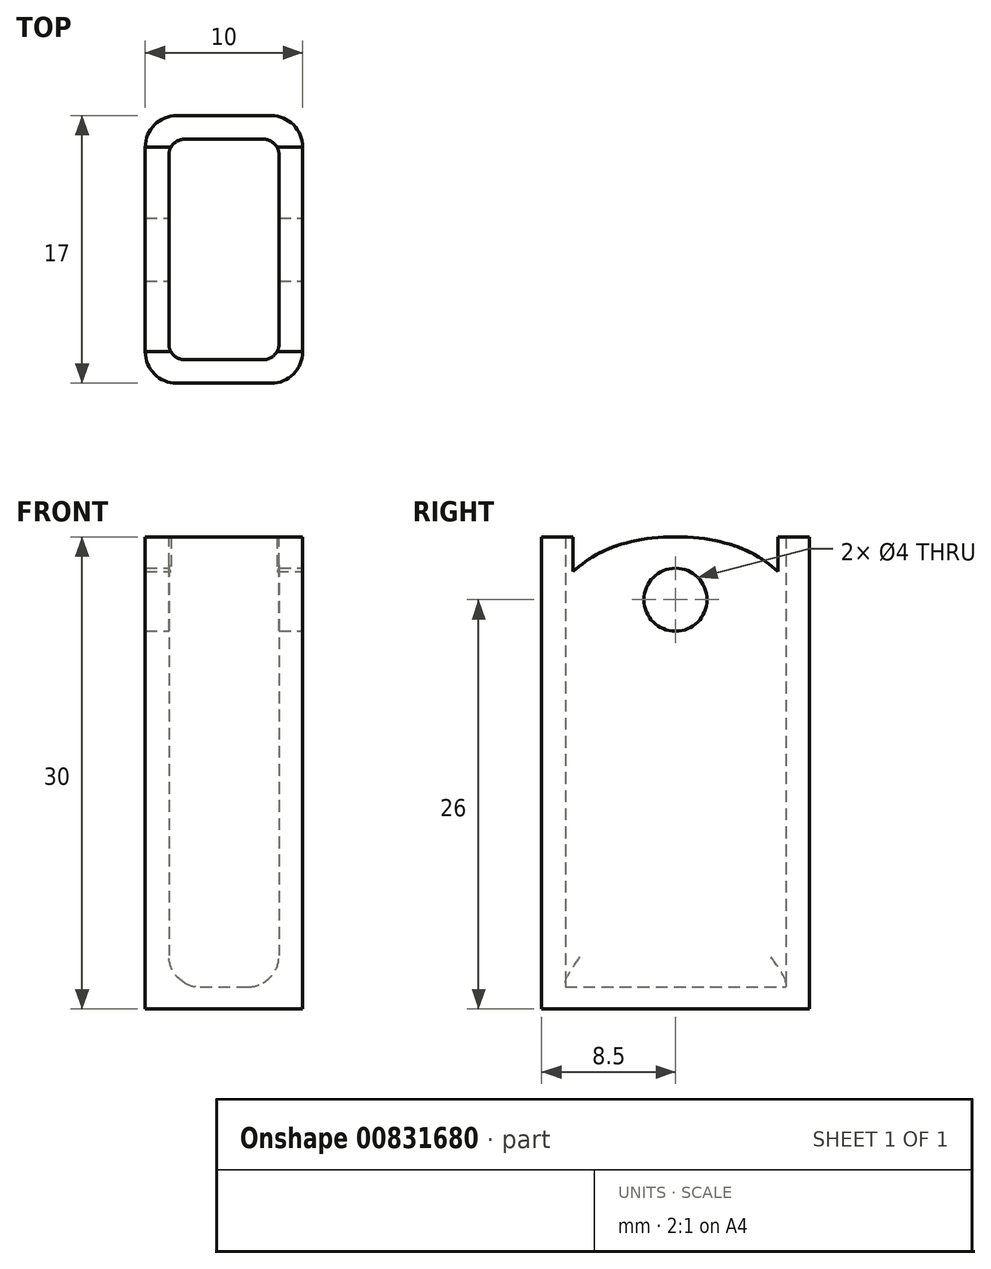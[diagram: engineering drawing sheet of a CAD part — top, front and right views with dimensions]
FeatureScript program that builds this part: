
annotation { "Feature Type Name" : "Feature", "Feature Type Description" : "" }
export const myFeature = defineFeature(function(context is Context, id is Id, definition is map)
    precondition{}
    {
        {
            var Q0;
            Q0=qCreatedBy(makeId("Top.planeOp"),FACE);
            var sketch = newSketch(context, id + "F0", { "sketchPlane" : qUnion([Q0])});
            skLineSegment(sketch, "E0.bottom", {"start": v(2.5, 7) * mm, "end": v(-2.5, 7) * mm});
            skLineSegment(sketch, "E0.top", {"start": v(2.5, -7) * mm, "end": v(-2.5, -7) * mm});
            skLineSegment(sketch, "E0.left", {"start": v(3.5, 6) * mm, "end": v(3.5, -6) * mm});
            skLineSegment(sketch, "E0.right", {"start": v(-3.5, 6) * mm, "end": v(-3.5, -6) * mm});
            skPoint(sketch, "E0.middle", {"position": v(0, 0) * mm});
            skLineSegment(sketch, "E1.0", {"start": v(3, 8.5) * mm, "end": v(-3, 8.5) * mm});
            skLineSegment(sketch, "E1.1", {"start": v(5, 6.5) * mm, "end": v(5, -6.5) * mm});
            skLineSegment(sketch, "E1.2", {"start": v(3, -8.5) * mm, "end": v(-3, -8.5) * mm});
            skLineSegment(sketch, "E1.3", {"start": v(-5, 6.5) * mm, "end": v(-5, -6.5) * mm});
            skPoint(sketch, "E2.visualSharp", {"position": v(-5, 8.5) * mm});
            skArc(sketch, "E2.filletArc", {"start": v(-3, 8.5) * mm, "mid": v(-4.41, 7.91) * mm, "end": v(-5, 6.5) * mm});
            skPoint(sketch, "E3.visualSharp", {"position": v(5, 8.5) * mm});
            skArc(sketch, "E3.filletArc", {"start": v(5, 6.5) * mm, "mid": v(4.41, 7.91) * mm, "end": v(3, 8.5) * mm});
            skPoint(sketch, "E4.visualSharp", {"position": v(5, -8.5) * mm});
            skArc(sketch, "E4.filletArc", {"start": v(3, -8.5) * mm, "mid": v(4.41, -7.91) * mm, "end": v(5, -6.5) * mm});
            skPoint(sketch, "E5.visualSharp", {"position": v(-5, -8.5) * mm});
            skArc(sketch, "E5.filletArc", {"start": v(-5, -6.5) * mm, "mid": v(-4.41, -7.91) * mm, "end": v(-3, -8.5) * mm});
            skPoint(sketch, "E6.visualSharp", {"position": v(3.5, -7) * mm});
            skArc(sketch, "E6.filletArc", {"start": v(2.5, -7) * mm, "mid": v(3.2, -6.7) * mm, "end": v(3.5, -6) * mm});
            skPoint(sketch, "E7.visualSharp", {"position": v(-3.5, -7) * mm});
            skArc(sketch, "E7.filletArc", {"start": v(-3.5, -6) * mm, "mid": v(-3.2, -6.7) * mm, "end": v(-2.5, -7) * mm});
            skPoint(sketch, "E8.visualSharp", {"position": v(-3.5, 7) * mm});
            skArc(sketch, "E8.filletArc", {"start": v(-2.5, 7) * mm, "mid": v(-3.2, 6.7) * mm, "end": v(-3.5, 6) * mm});
            skPoint(sketch, "E9.visualSharp", {"position": v(3.5, 7) * mm});
            skArc(sketch, "E9.filletArc", {"start": v(3.5, 6) * mm, "mid": v(3.2, 6.7) * mm, "end": v(2.5, 7) * mm});
            skSolve(sketch);
        }
        {
            var Q0;
            Q0=makeQuery(id+"F0.imprint","IMPRINT",FACE,{"disambiguationData":[TD([[makeQuery(id+"F0.imprint","IMPRINT",EDGE,{"derivedFrom":sQuery(id+"F0.wireOp",EDGE,"E0.bottom")}),1.0]])]});
            var Q1;
            Q1=makeQuery(id+"F0.imprint","IMPRINT",FACE,{"disambiguationData":[TD([[makeQuery(id+"F0.imprint","IMPRINT",EDGE,{"derivedFrom":sQuery(id+"F0.wireOp",EDGE,"E0.bottom")}),-1.0]])]});
            extrude(context, id + "F1", {"entities" : qUnion([Q0, Q1]), "depth" : 1.4 * mm, "offsetDistance" : 25 * mm});
        }
        {
            var Q0;
            Q0=makeQuery(id+"F0.imprint","IMPRINT",FACE,{"disambiguationData":[TD([[makeQuery(id+"F0.imprint","IMPRINT",EDGE,{"derivedFrom":sQuery(id+"F0.wireOp",EDGE,"E0.bottom")}),-1.0]])]});
            extrude(context, id + "F2", {"entities" : qUnion([Q0]), "operationType" : NewBodyOperationType.ADD, "depth" : 30 * mm, "offsetDistance" : 25 * mm});
        }
        {
            var Q0;
            {var subQ0=sQuery(id+"F0.wireOp",EDGE,"E1.1");Q0=makeQuery(id+"F2.boolean.opBoolean","MERGE",FACE,{"derivedFrom":[makeQuery(id+"F1.opExtrude","SWEPT_FACE",FACE,{"disambiguationData":[OSD([subQ0])]}),makeQuery(id+"F2.opExtrude","SWEPT_FACE",FACE,{"disambiguationData":[OSD([subQ0])]})]});}
            var sketch = newSketch(context, id + "F3", { "sketchPlane" : qUnion([Q0])});
            skCircle(sketch, "E10", {"center": v(0, 26) * mm, "radius": 2 * mm});
            skPoint(sketch, "E10.centerSnap0", {"position": v(0, 30) * mm});
            skLineSegment(sketch, "E11", {"start": v(-18.62, 23) * mm, "end": v(23.8, 23) * mm, "construction": true});
            skLineSegment(sketch, "E12.0", {"start": v(-8.5, 30) * mm, "end": v(-8.5, 0) * mm});
            skLineSegment(sketch, "E13.0", {"start": v(8.5, 30) * mm, "end": v(8.5, 0) * mm});
            skFitSpline(sketch, "E14", {"points": [v(-8.5, 23) * mm, v(0, 30) * mm], "startDerivative": vector(0, 10.43) * mm, "endDerivative": vector(17.83, 0) * mm});
            skFitSpline(sketch, "E15.MirrorCS", {"points": [v(8.5, 23) * mm, v(0, 30) * mm], "startDerivative": vector(0, 10.43) * mm, "endDerivative": vector(-17.83, 0) * mm});
            skLineSegment(sketch, "E16", {"start": v(-8.5, 23) * mm, "end": v(-8.5, 30) * mm});
            skLineSegment(sketch, "E17", {"start": v(8.5, 30) * mm, "end": v(8.5, 23) * mm});
            skLineSegment(sketch, "E18", {"start": v(-8.5, 30) * mm, "end": v(8.5, 30) * mm});
            skLineSegment(sketch, "E19.0.0", {"start": v(-6, 1.4) * mm, "end": v(-7, 1.4) * mm});
            skLineSegment(sketch, "E19.0.1", {"start": v(-6, 1.4) * mm, "end": v(6, 1.4) * mm});
            skLineSegment(sketch, "E19.0.2", {"start": v(7, 1.4) * mm, "end": v(6, 1.4) * mm});
            skLineSegment(sketch, "E19.0.4", {"start": v(6, 1.4) * mm, "end": v(7, 1.4) * mm});
            skLineSegment(sketch, "E19.0.5", {"start": v(6, 1.4) * mm, "end": v(-6, 1.4) * mm});
            skLineSegment(sketch, "E19.0.6", {"start": v(-7, 1.4) * mm, "end": v(-6, 1.4) * mm});
            skSolve(sketch);
        }
        {
            var Q0;
            {var subQ0=sQuery(id+"F3.wireOp",EDGE,"E16");Q0=makeQuery(id+"F3.imprint","IMPRINT",FACE,{"disambiguationData":[TD([[makeQuery(id+"F3.imprint","IMPRINT",EDGE,{"derivedFrom":subQ0}),-1.0]])]});}
            var Q1;
            {var subQ0=sQuery(id+"F3.wireOp",EDGE,"E18");var subQ1=sQuery(id+"F3.wireOp",EDGE,"E14");var subQ2=makeQuery(id+"F3.imprint","INTERSECT",VERTEX,{"derivedFrom":[subQ1,sQuery(id+"F3.wireOp",EDGE,"E15.MirrorCS"),subQ0]});Q1=makeQuery(id+"F3.imprint","IMPRINT",FACE,{"disambiguationData":[TD([[makeQuery(id+"F3.imprint","IMPRINT",EDGE,{"disambiguationData":[TD([[subQ2,1.0]])],"derivedFrom":subQ1}),1.0]])]});}
            var Q2;
            {var subQ0=sQuery(id+"F3.wireOp",EDGE,"E18");var subQ1=sQuery(id+"F3.wireOp",EDGE,"E15.MirrorCS");var subQ2=makeQuery(id+"F3.imprint","INTERSECT",VERTEX,{"derivedFrom":[sQuery(id+"F3.wireOp",EDGE,"E14"),subQ1,subQ0]});Q2=makeQuery(id+"F3.imprint","IMPRINT",FACE,{"disambiguationData":[TD([[makeQuery(id+"F3.imprint","IMPRINT",EDGE,{"disambiguationData":[TD([[subQ2,1.0]])],"derivedFrom":subQ1}),-1.0]])]});}
            var Q3;
            {var subQ0=sQuery(id+"F3.wireOp",EDGE,"E17");Q3=makeQuery(id+"F3.imprint","IMPRINT",FACE,{"disambiguationData":[TD([[makeQuery(id+"F3.imprint","IMPRINT",EDGE,{"derivedFrom":subQ0}),-1.0]])]});}
            var Q4;
            Q4=makeQuery(id+"F3.imprint","IMPRINT",FACE,{"disambiguationData":[TD([[makeQuery(id+"F3.imprint","IMPRINT",EDGE,{"derivedFrom":sQuery(id+"F3.wireOp",EDGE,"E10")}),1.0]])]});
            extrude(context, id + "F4", {"entities" : qUnion([Q0, Q1, Q2, Q3, Q4]), "operationType" : NewBodyOperationType.REMOVE, "endBound" : BoundingType.THROUGH_ALL, "oppositeDirection" : true, "depth" : 25 * mm, "offsetDistance" : 25 * mm});
        }
        {
            var Q0;
            Q0=makeQuery(id+"F2.boolean.opBoolean","INTERSECT",EDGE,{"derivedFrom":[makeQuery(id+"F1.opExtrude","CAP_FACE",FACE,{"disambiguationData":[OSD([sQuery(id+"F0.wireOp",EDGE,"E1.0"),sQuery(id+"F0.wireOp",EDGE,"E1.1"),sQuery(id+"F0.wireOp",EDGE,"E1.2"),sQuery(id+"F0.wireOp",EDGE,"E1.3"),sQuery(id+"F0.wireOp",EDGE,"E2.filletArc"),sQuery(id+"F0.wireOp",EDGE,"E3.filletArc"),sQuery(id+"F0.wireOp",EDGE,"E4.filletArc"),sQuery(id+"F0.wireOp",EDGE,"E5.filletArc")])],"isStart":false}),makeQuery(id+"F2.opExtrude","SWEPT_FACE",FACE,{"disambiguationData":[OSD([sQuery(id+"F0.wireOp",EDGE,"E0.left")])]})]});
            var Q1;
            Q1=makeQuery(id+"F2.boolean.opBoolean","INTERSECT",EDGE,{"derivedFrom":[makeQuery(id+"F1.opExtrude","CAP_FACE",FACE,{"disambiguationData":[OSD([sQuery(id+"F0.wireOp",EDGE,"E1.0"),sQuery(id+"F0.wireOp",EDGE,"E1.1"),sQuery(id+"F0.wireOp",EDGE,"E1.2"),sQuery(id+"F0.wireOp",EDGE,"E1.3"),sQuery(id+"F0.wireOp",EDGE,"E2.filletArc"),sQuery(id+"F0.wireOp",EDGE,"E3.filletArc"),sQuery(id+"F0.wireOp",EDGE,"E4.filletArc"),sQuery(id+"F0.wireOp",EDGE,"E5.filletArc")])],"isStart":false}),makeQuery(id+"F2.opExtrude","SWEPT_FACE",FACE,{"disambiguationData":[OSD([sQuery(id+"F0.wireOp",EDGE,"E0.right")])]})]});
            fillet(context, id + "F5", {"entities" : qUnion([Q0, Q1]), "radius" : 2 * mm, "allowEdgeOverflow" : false});
        }
    });
